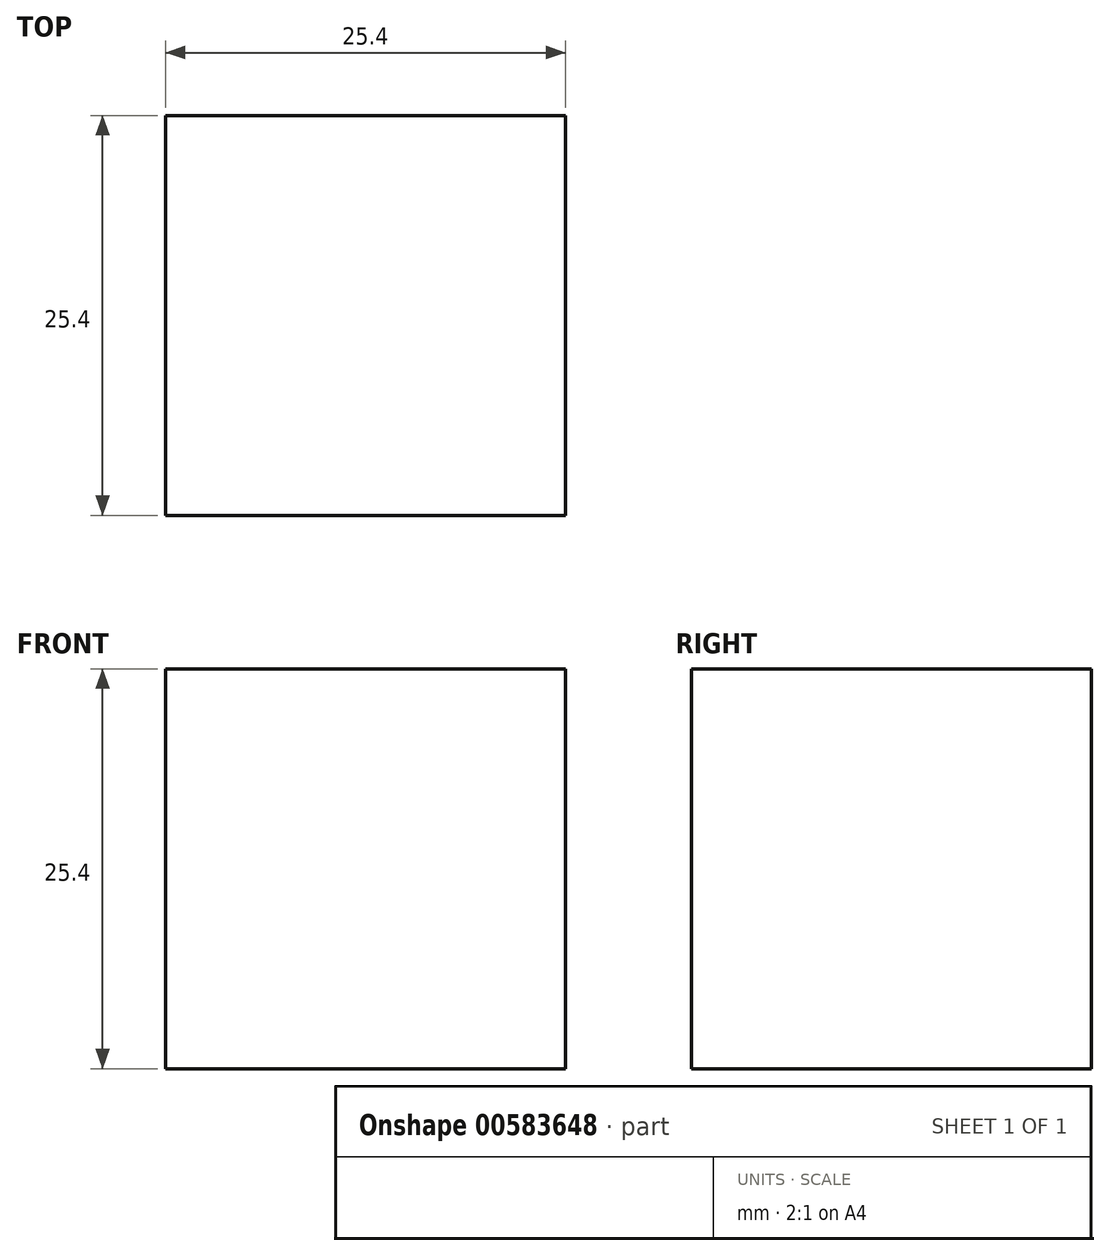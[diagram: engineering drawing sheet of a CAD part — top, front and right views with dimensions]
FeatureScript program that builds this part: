
annotation { "Feature Type Name" : "Feature", "Feature Type Description" : "" }
export const myFeature = defineFeature(function(context is Context, id is Id, definition is map)
    precondition{}
    {
        {
            var Q0;
            Q0=qCreatedBy(makeId("Front.planeOp"),FACE);
            var sketch = newSketch(context, id + "F0", { "sketchPlane" : qUnion([Q0])});
            skLineSegment(sketch, "E0.bottom", {"start": v(-20.22, 10.14) * mm, "end": v(5.18, 10.14) * mm});
            skLineSegment(sketch, "E0.top", {"start": v(-20.22, -15.26) * mm, "end": v(5.18, -15.26) * mm});
            skLineSegment(sketch, "E0.left", {"start": v(-20.22, 10.14) * mm, "end": v(-20.22, -15.26) * mm});
            skLineSegment(sketch, "E0.right", {"start": v(5.18, 10.14) * mm, "end": v(5.18, -15.26) * mm});
            skSolve(sketch);
        }
        {
            var Q0;
            Q0=makeQuery(id+"F0.imprint","IMPRINT",FACE,{"disambiguationData":[TD([[makeQuery(id+"F0.imprint","IMPRINT",EDGE,{"derivedFrom":sQuery(id+"F0.wireOp",EDGE,"E0.bottom")}),-1.0]])]});
            extrude(context, id + "F1", {"entities" : qUnion([Q0]), "depth" : 25.4 * mm, "offsetDistance" : 25.4 * mm});
        }
    });
